# Revit family: LeL Colorado 6.2
name_source: partatom
category: Lighting Fixtures
units: mm (PartAtom-declared; Revit-internal decimal feet)

## family parameters
Always vertical = No
Cut with Voids When Loaded = No
Light Source = No
OmniClass Number = 23.80.70.00
OmniClass Title = Lighting
Part Type = Normal
Room Calculation Point = No
Round Connector Dimension = Use Diameter
Shared = No
Work Plane-Based = Yes

## types (6) — shared parameters
Alimentazione = 230 V
Apparent Load = 85 VA
CCT = 3000 K
CRI = CRI80
Default Elevation = 1219 mm
Description = Outdoor/projectors
Finish = LeL Black
IK = IK09
IP = IP65 IP67 IP69
Lamp = LED
Manufacturer = L&L Luce&Light srl
Model = CA62
Rated Power supply = 230 V
URL = https://www.lucelight.it
Wattage = 85 W
Weight = 10.00 kg

## per-type parameters (varying)
| type | Lumen Output | Optic |
| 6.2 W 13°x65° 85W | 5072 lm | COLORADO Light source : 6.2 W 13°x65° 85W |
| 6.2 D 85W | 2853 lm | COLORADO Light source : 6.2 D 85W |
| 6.2 L 37° 85W | 3761 lm | COLORADO Light source : 6.2 L 37° 85W |
| 6.2 M 25° 85W | 5104 lm | COLORADO Light source : 6.2 M 25° 85W |
| 6.2 S 15° 85W | 4758 lm | COLORADO Light source : 6.2 S 15° 85W |
| 6.2 X 65°x13° 85W | 5072 lm | COLORADO Light source : 6.2 X 65°x13° 85W |

## geometry (parser evidence)
native form markers: Sweep x4
no freeform markers — native parametric forms only
